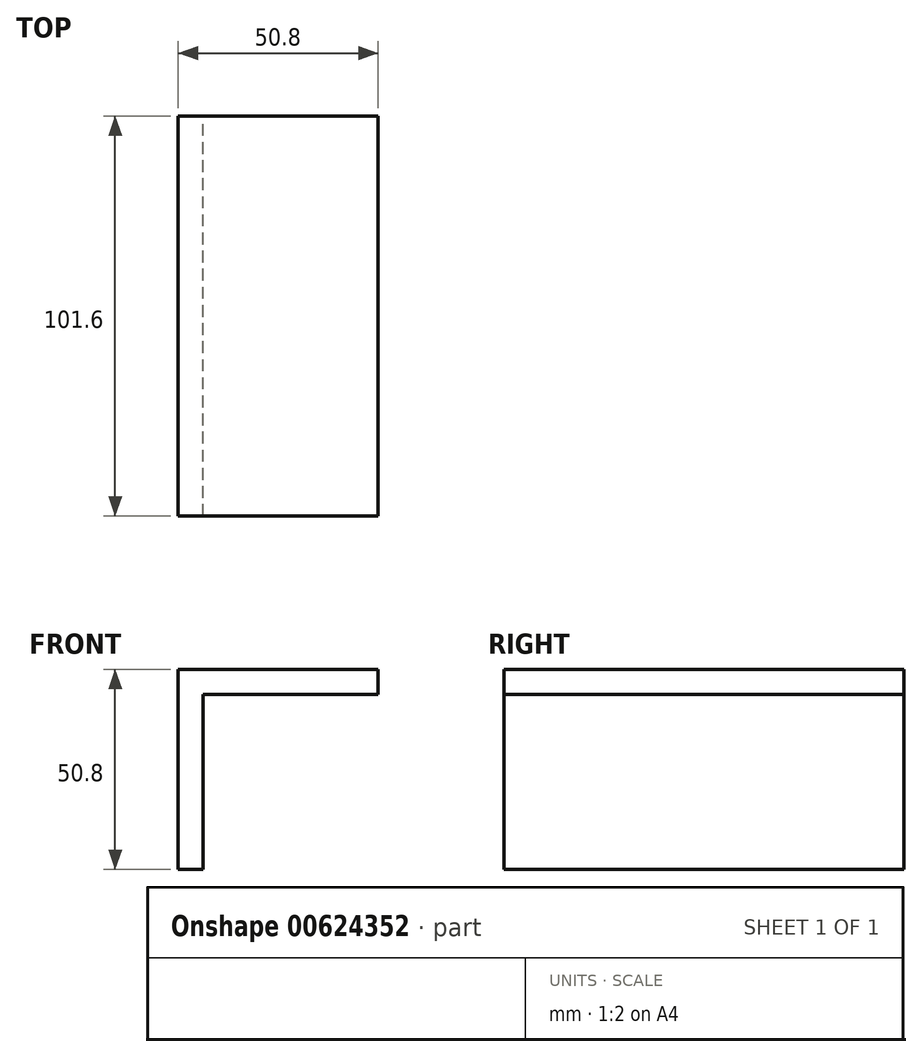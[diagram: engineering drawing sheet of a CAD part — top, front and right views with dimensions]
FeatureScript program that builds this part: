
annotation { "Feature Type Name" : "Feature", "Feature Type Description" : "" }
export const myFeature = defineFeature(function(context is Context, id is Id, definition is map)
    precondition{}
    {
        {
            var Q0;
            Q0=qCreatedBy(makeId("Front.planeOp"),FACE);
            var sketch = newSketch(context, id + "F0", { "sketchPlane" : qUnion([Q0])});
            skLineSegment(sketch, "E0.bottom", {"start": v(3.18, -25.4) * mm, "end": v(-3.17, -25.4) * mm});
            skLineSegment(sketch, "E0.top", {"start": v(3.17, 25.4) * mm, "end": v(-3.18, 25.4) * mm});
            skLineSegment(sketch, "E0.left", {"start": v(3.18, -25.4) * mm, "end": v(3.18, 19.05) * mm});
            skLineSegment(sketch, "E0.right", {"start": v(-3.17, -25.4) * mm, "end": v(-3.18, 25.4) * mm});
            skPoint(sketch, "E0.middle", {"position": v(0, 0) * mm});
            skLineSegment(sketch, "E1.bottom", {"start": v(-3.18, 25.4) * mm, "end": v(47.63, 25.4) * mm});
            skLineSegment(sketch, "E1.top", {"start": v(3.18, 19.05) * mm, "end": v(47.62, 19.05) * mm});
            skLineSegment(sketch, "E1.left", {"start": v(-3.18, 25.4) * mm, "end": v(-3.18, 19.05) * mm});
            skLineSegment(sketch, "E1.right", {"start": v(47.63, 25.4) * mm, "end": v(47.63, 19.05) * mm});
            skSolve(sketch);
        }
        {
            var Q0;
            Q0=makeQuery(id+"F0.imprint","IMPRINT",FACE,{"disambiguationData":[TD([[makeQuery(id+"F0.imprint","IMPRINT",EDGE,{"derivedFrom":sQuery(id+"F0.wireOp",EDGE,"E0.bottom")}),-1.0]])]});
            extrude(context, id + "F1", {"entities" : qUnion([Q0]), "depth" : 101.6 * mm, "offsetDistance" : 25.4 * mm});
        }
    });
